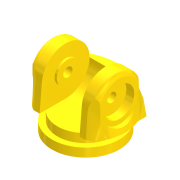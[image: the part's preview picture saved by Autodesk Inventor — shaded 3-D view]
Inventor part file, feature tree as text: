
AUTODESK INVENTOR PART (.ipt)
format: ipt  version: 2020 (Build 240168000, 168)  size: 811,520 bytes
history: native  units: mm
features: sketch x17, extrude x14, projected_geometry x4, mirror x3, other x3, loft x2, plane x2, fillet x1, direct_edit x1
ambient origin geometry x8: Origin, YZ Plane, XZ Plane, XY Plane, X Axis, Y Axis, Z Axis, Center Point
bodies: Solid1 (feature_tree)
feature tree (47):
  extrude  "Extrusion1"  Depth=2.0mm TaperAngle=0.0deg
  extrude  "Extrusion2"  Depth=2.0mm TaperAngle=0.0deg
  extrude  "Extrusion3"  Depth=11.0mm
  loft  "Loft1"
  sketch  "Sketch6"  dims[d58=-5.5mm d59=0.0mm]
  plane  "Work Plane1"
  loft  "Loft2"
  extrude  "Extrusion4"  TaperAngle=0.0deg  [1 undecoded]
  extrude  "Extrusion5"  TaperAngle=0.0deg  [1 undecoded]
  fillet  "Fillet1"  Radius=12.0mm
  extrude  "Extrusion6"  Depth=1.0mm
  extrude  "Extrusion7"  Depth=8.75mm TaperAngle=0.0deg
  extrude  "Extrusion8"  Depth=13.0mm
  extrude  "Extrusion9"  Depth=5.1mm
  mirror  "Mirror1"
  extrude  "Extrusion10"  Depth=2.12mm
  extrude  "Extrusion11"  Depth=6.75mm
  mirror  "Mirror2"
  extrude  "Extrusion12"  Depth=8.8mm
  mirror  "Mirror3"
  extrude  "Extrusion13"  Depth=11.0mm
  extrude  "Extrusion17"  Depth=2.1mm
  direct_edit  "Direct Edit1"
  sketch  "Sketch1"  dims[d0=15.5mm d1=2.0mm d2=0.0mm]
  sketch  "Sketch2"  dims[d3=12.0mm d4=2.0mm d5=0.0mm]
  sketch  "Sketch3"  dims[d6=5.5mm d7=11.0mm]
  sketch  "Sketch4"  dims[d8=12.0mm d9=0.0mm d38=0.0mm d39=90.0deg]
  other  "Image1"
  sketch  "Sketch5"  dims[d40=0.0mm d41=90.0deg d49=0.0mm]
  other  "Image2"
  projected_geometry  "Projected Loop1"
  sketch  "Sketch7"  dims[d60=0.0mm d61=90.0deg d62=0.0mm d63=90.0deg d64=12.0mm d65=0.0mm]
  projected_geometry  "Projected Loop2"
  sketch  "Sketch8"  dims[d66=7.792mm d67=0.0mm d68=1.0mm]
  projected_geometry  "Projected Loop3"
  sketch  "Sketch9"  dims[d69=4.6mm d70=8.75mm d71=5.5mm d72=0.0mm d73=0.0mm]
  projected_geometry  "Projected Loop4"
  sketch  "Sketch10"  dims[d74=4.0mm d75=0.0mm d76=13.0mm]
  sketch  "Sketch11"  dims[d77=2.0mm d78=0.0mm d79=5.1mm]
  sketch  "Sketch12"  dims[d80=0.5mm d81=0.0mm d82=2.12mm]
  sketch  "Sketch13"  dims[d83=12.236mm d84=0.0mm d85=6.75mm]
  plane  "Work Plane2"
  sketch  "Sketch14"  dims[d86=2.9mm d87=1.8mm d88=0.0mm d89=0.0mm d90=8.8mm]
  sketch  "Sketch15"  dims[d91=2.9mm d92=0.0mm d93=11.0mm]
  sketch  "Sketch16"  dims[d94=4.9mm d95=0.0mm d109=2.1mm]
  sketch  "Sketch21"  dims[d110=0.0mm d111=0.0mm d112=8.0mm d113=10.0mm d114=10.0mm]
  other  "Scale1"
note: 2 required parameter values undecoded (feature->parameter linkage not recoverable at this tier; creation-order binding heuristic only, values carry confidence <= 0.55)
